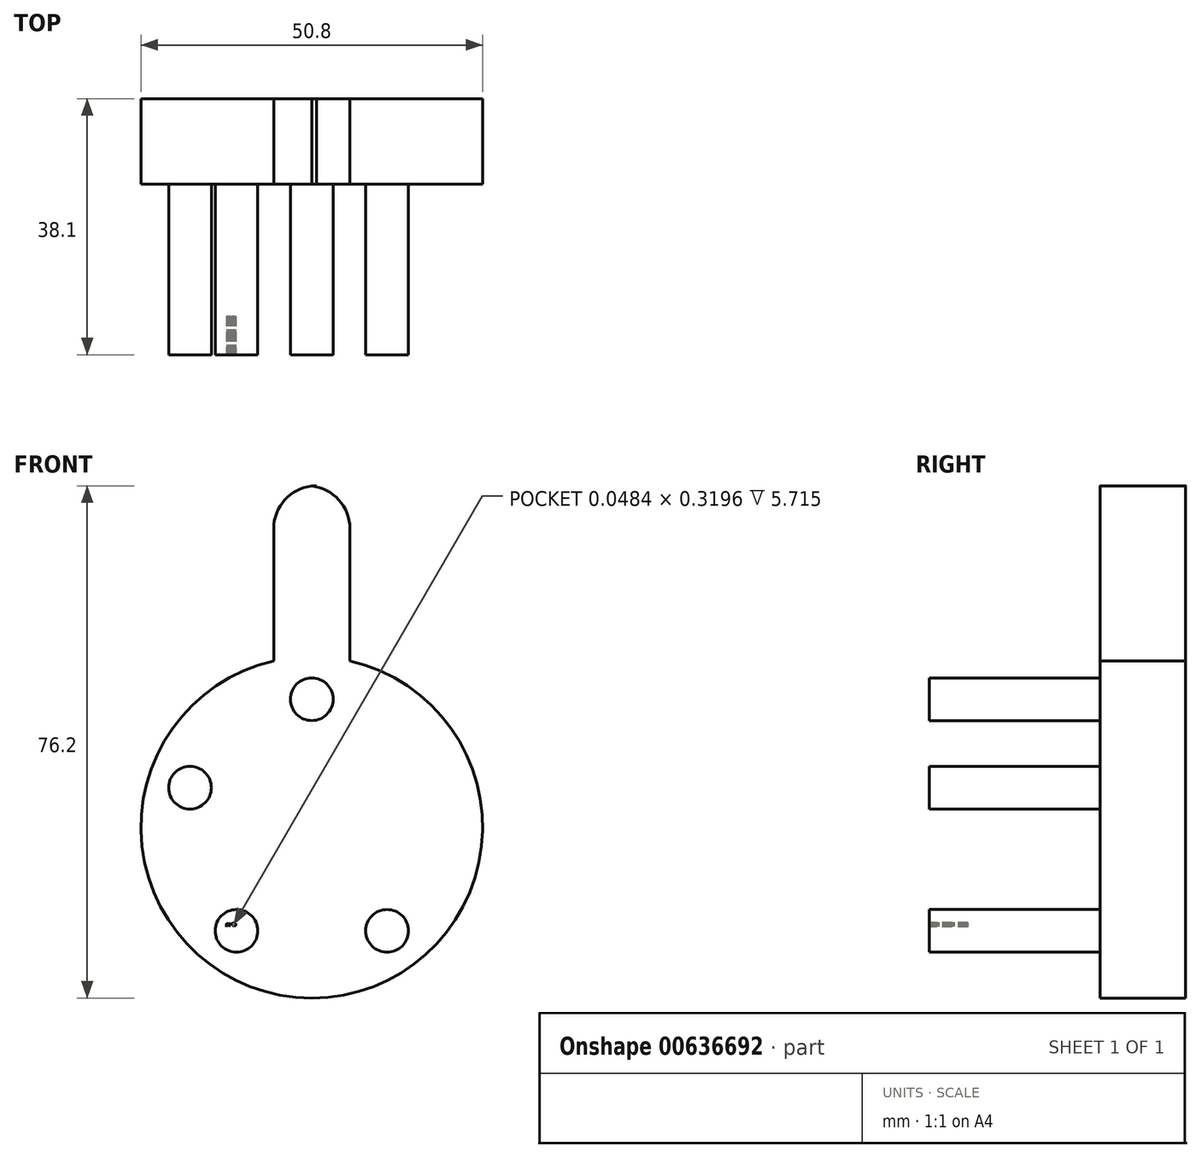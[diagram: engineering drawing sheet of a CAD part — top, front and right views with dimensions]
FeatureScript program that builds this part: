
annotation { "Feature Type Name" : "Feature", "Feature Type Description" : "" }
export const myFeature = defineFeature(function(context is Context, id is Id, definition is map)
    precondition{}
    {
        {
            var Q0;
            Q0=qCreatedBy(makeId("Front.planeOp"),FACE);
            var sketch = newSketch(context, id + "F0", { "sketchPlane" : qUnion([Q0])});
            skCircle(sketch, "E0", {"center": v(0, 0) * mm, "radius": 25.4 * mm});
            skLineSegment(sketch, "E1", {"start": v(0, 25.4) * mm, "end": v(0, 50.8) * mm});
            skLineSegment(sketch, "E2", {"start": v(0.69, 50.8) * mm, "end": v(0, 50.8) * mm});
            skLineSegment(sketch, "E3", {"start": v(-5.66, 44.45) * mm, "end": v(-5.66, 24.76) * mm});
            skPoint(sketch, "E4.visualSharp", {"position": v(-5.66, 50.8) * mm});
            skArc(sketch, "E4.filletArc", {"start": v(0.69, 50.8) * mm, "mid": v(-3.8, 48.94) * mm, "end": v(-5.66, 44.45) * mm});
            skPoint(sketch, "E5.MirrorP", {"position": v(5.66, 50.8) * mm});
            skLineSegment(sketch, "E6.MirrorCS", {"start": v(5.66, 44.45) * mm, "end": v(5.66, 24.76) * mm});
            skArc(sketch, "E7.MirrorCS", {"start": v(-0.69, 50.8) * mm, "mid": v(3.8, 48.94) * mm, "end": v(5.66, 44.45) * mm});
            skSolve(sketch);
        }
        {
            var Q0;
            Q0 = qSketchRegion(id + "F0", true);
            extrude(context, id + "F1", {"entities" : qUnion([Q0]), "depth" : 12.7 * mm, "offsetDistance" : 25.4 * mm});
        }
        {
            var Q0;
            Q0=makeQuery(id+"F1.opExtrude","CAP_FACE",FACE,{"disambiguationData":[OSD([sQuery(id+"F0.wireOp",EDGE,"E0")])],"isStart":false});
            var sketch = newSketch(context, id + "F2", { "sketchPlane" : qUnion([Q0])});
            skLineSegment(sketch, "E8", {"start": v(0, 25.4) * mm, "end": v(0, 19.05) * mm});
            skCircle(sketch, "E9", {"center": v(0, 19.05) * mm, "radius": 3.18 * mm});
            skCircle(sketch, "E10.1.0", {"center": v(-18.12, 5.89) * mm, "radius": 3.18 * mm});
            skCircle(sketch, "E10.2.0", {"center": v(-11.2, -15.41) * mm, "radius": 3.18 * mm});
            skCircle(sketch, "E10.3.0", {"center": v(11.2, -15.41) * mm, "radius": 3.18 * mm});
            skPoint(sketch, "E10.center", {"position": v(0, 0) * mm});
            skCircle(sketch, "E11.1.4.0", {"center": v(18.12, 5.89) * mm, "radius": 3.18 * mm});
            skSolve(sketch);
        }
        {
            var Q0;
            Q0=makeQuery(id+"F2.imprint","IMPRINT",FACE,{"disambiguationData":[TD([[makeQuery(id+"F2.imprint","IMPRINT",EDGE,{"derivedFrom":sQuery(id+"F2.wireOp",EDGE,"E10.5.0")}),1.0]])]});
            var Q1;
            Q1=makeQuery(id+"F2.imprint","IMPRINT",FACE,{"disambiguationData":[TD([[makeQuery(id+"F2.imprint","IMPRINT",EDGE,{"derivedFrom":sQuery(id+"F2.wireOp",EDGE,"E9")}),1.0]])]});
            var Q2;
            Q2=makeQuery(id+"F2.imprint","IMPRINT",FACE,{"disambiguationData":[TD([[makeQuery(id+"F2.imprint","IMPRINT",EDGE,{"derivedFrom":sQuery(id+"F2.wireOp",EDGE,"E10.1.0")}),1.0]])]});
            var Q3;
            Q3=makeQuery(id+"F2.imprint","IMPRINT",FACE,{"disambiguationData":[TD([[makeQuery(id+"F2.imprint","IMPRINT",EDGE,{"derivedFrom":sQuery(id+"F2.wireOp",EDGE,"E10.4.0")}),1.0]])]});
            var Q4;
            Q4=makeQuery(id+"F2.imprint","IMPRINT",FACE,{"disambiguationData":[TD([[makeQuery(id+"F2.imprint","IMPRINT",EDGE,{"derivedFrom":sQuery(id+"F2.wireOp",EDGE,"E10.3.0")}),1.0]])]});
            var Q5;
            Q5=makeQuery(id+"F2.imprint","IMPRINT",FACE,{"disambiguationData":[TD([[makeQuery(id+"F2.imprint","IMPRINT",EDGE,{"derivedFrom":sQuery(id+"F2.wireOp",EDGE,"E10.2.0")}),1.0]])]});
            var Q6;
            Q6=makeQuery(id+"F2.imprint","IMPRINT",FACE,{"disambiguationData":[TD([[makeQuery(id+"F2.imprint","IMPRINT",EDGE,{"derivedFrom":sQuery(id+"F2.wireOp",EDGE,"3d855112-aa8d-4504-a31c-7981520b6fd2.1.7.0")}),1.0]])]});
            var Q7;
            Q7=makeQuery(id+"F2.imprint","IMPRINT",FACE,{"disambiguationData":[TD([[makeQuery(id+"F2.imprint","IMPRINT",EDGE,{"derivedFrom":sQuery(id+"F2.wireOp",EDGE,"3d855112-aa8d-4504-a31c-7981520b6fd2.1.6.0")}),1.0]])]});
            var Q8;
            Q8=makeQuery(id+"F2.imprint","IMPRINT",FACE,{"disambiguationData":[TD([[makeQuery(id+"F2.imprint","IMPRINT",EDGE,{"derivedFrom":sQuery(id+"F2.wireOp",EDGE,"fa8cfa11-95dc-4c43-ba04-833ef0709e26.1.13.0")}),1.0]])]});
            var Q9;
            Q9=makeQuery(id+"F2.imprint","IMPRINT",FACE,{"disambiguationData":[TD([[makeQuery(id+"F2.imprint","IMPRINT",EDGE,{"derivedFrom":sQuery(id+"F2.wireOp",EDGE,"fa8cfa11-95dc-4c43-ba04-833ef0709e26.1.12.0")}),1.0]])]});
            var Q10;
            Q10=makeQuery(id+"F2.imprint","IMPRINT",FACE,{"disambiguationData":[TD([[makeQuery(id+"F2.imprint","IMPRINT",EDGE,{"derivedFrom":sQuery(id+"F2.wireOp",EDGE,"fa8cfa11-95dc-4c43-ba04-833ef0709e26.1.11.0")}),1.0]])]});
            var Q11;
            Q11=makeQuery(id+"F2.imprint","IMPRINT",FACE,{"disambiguationData":[TD([[makeQuery(id+"F2.imprint","IMPRINT",EDGE,{"derivedFrom":sQuery(id+"F2.wireOp",EDGE,"fa8cfa11-95dc-4c43-ba04-833ef0709e26.1.10.0")}),1.0]])]});
            var Q12;
            Q12=makeQuery(id+"F2.imprint","IMPRINT",FACE,{"disambiguationData":[TD([[makeQuery(id+"F2.imprint","IMPRINT",EDGE,{"derivedFrom":sQuery(id+"F2.wireOp",EDGE,"fa8cfa11-95dc-4c43-ba04-833ef0709e26.1.9.0")}),1.0]])]});
            var Q13;
            Q13=makeQuery(id+"F2.imprint","IMPRINT",FACE,{"disambiguationData":[TD([[makeQuery(id+"F2.imprint","IMPRINT",EDGE,{"derivedFrom":sQuery(id+"F2.wireOp",EDGE,"fa8cfa11-95dc-4c43-ba04-833ef0709e26.1.8.0")}),1.0]])]});
            var Q14;
            Q14=makeQuery(id+"F2.imprint","IMPRINT",FACE,{"disambiguationData":[TD([[makeQuery(id+"F2.imprint","IMPRINT",EDGE,{"derivedFrom":sQuery(id+"F2.wireOp",EDGE,"fa8cfa11-95dc-4c43-ba04-833ef0709e26.1.15.0")}),1.0]])]});
            var Q15;
            Q15=makeQuery(id+"F2.imprint","IMPRINT",FACE,{"disambiguationData":[TD([[makeQuery(id+"F2.imprint","IMPRINT",EDGE,{"derivedFrom":sQuery(id+"F2.wireOp",EDGE,"fa8cfa11-95dc-4c43-ba04-833ef0709e26.1.14.0")}),1.0]])]});
            extrude(context, id + "F3", {"entities" : qUnion([Q0, Q1, Q2, Q3, Q4, Q5, Q6, Q7, Q8, Q9, Q10, Q11, Q12, Q13, Q14, Q15]), "operationType" : NewBodyOperationType.ADD, "depth" : 25.4 * mm, "offsetDistance" : 25.4 * mm});
        }
        {
            var Q0;
            Q0=makeQuery(id+"F3.opExtrude","CAP_FACE",FACE,{"disambiguationData":[OSD([sQuery(id+"F2.wireOp",EDGE,"E10.2.0")])],"isStart":false});
            var sketch = newSketch(context, id + "F4", { "sketchPlane" : qUnion([Q0])});
            skText(sketch, "E12", { "text": "penis\n", "fontName": "OpenSans-Regular.ttf"});
            const initialGuessF4  = {"E12": [-0.01277, -0.01465, 1, 0, 0.00043]};
            skSetInitialGuess(sketch, initialGuessF4);
            skSolve(sketch);
        }
        {
            var Q0;
            Q0 = qSketchRegion(id + "F4", true);
            extrude(context, id + "F5", {"entities" : qUnion([Q0]), "operationType" : NewBodyOperationType.REMOVE, "oppositeDirection" : true, "depth" : 5.7 * mm, "offsetDistance" : 25.4 * mm});
        }
    });
